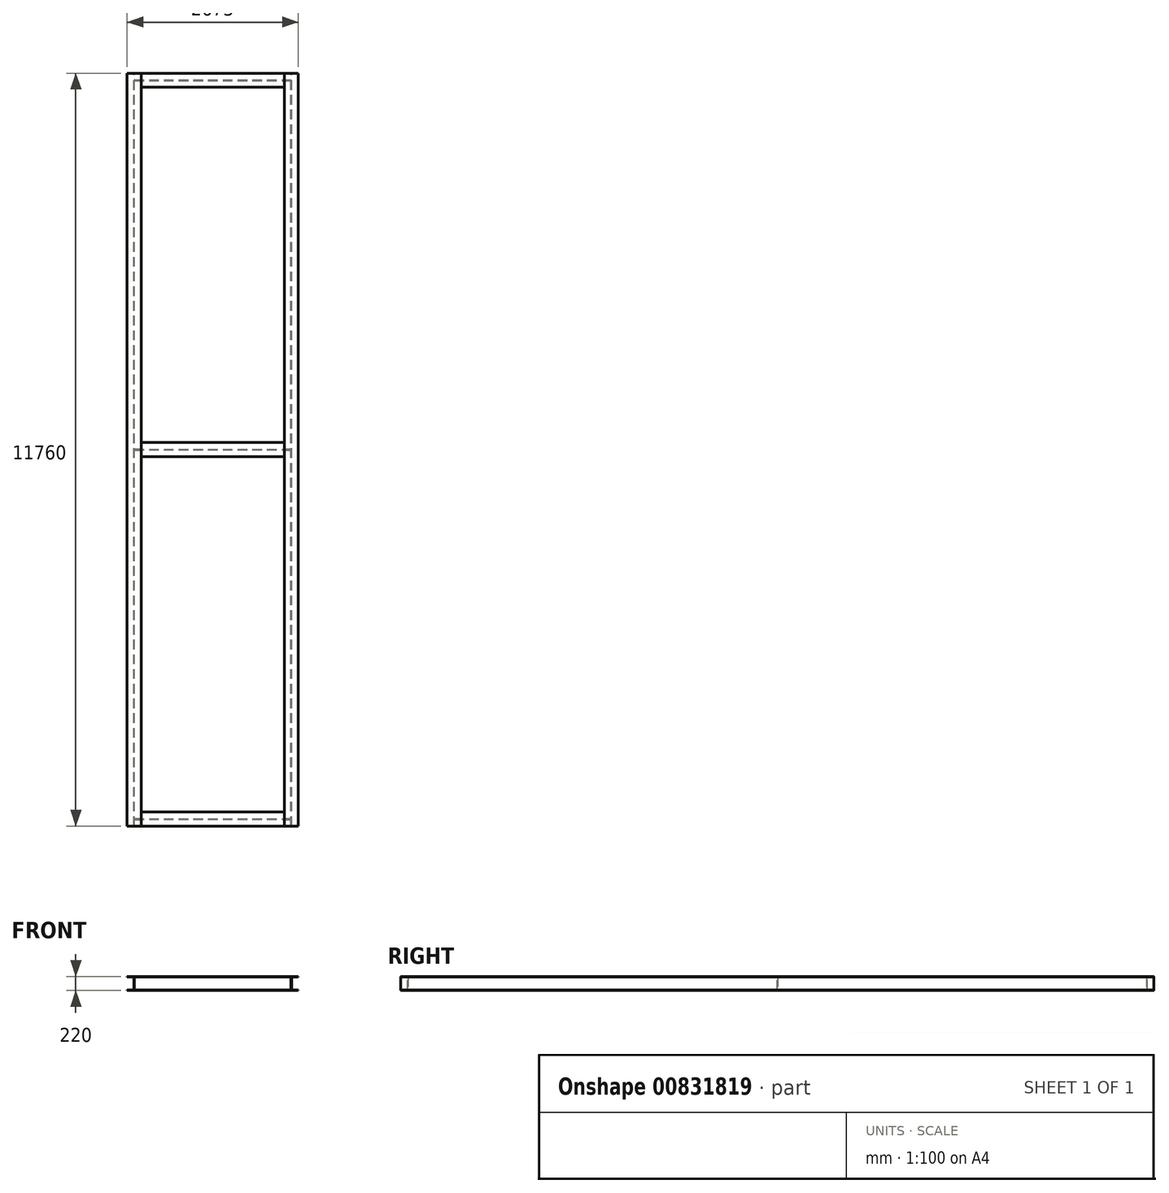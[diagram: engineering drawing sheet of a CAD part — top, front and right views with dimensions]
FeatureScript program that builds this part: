
annotation { "Feature Type Name" : "Feature", "Feature Type Description" : "" }
export const myFeature = defineFeature(function(context is Context, id is Id, definition is map)
    precondition{}
    {
        {
            var Q0;
            Q0=qCreatedBy(makeId("Front.planeOp"),FACE);
            var sketch = newSketch(context, id + "F0", { "sketchPlane" : qUnion([Q0])});
            skLineSegment(sketch, "E0", {"start": v(0, 0) * mm, "end": v(0, 110) * mm, "construction": true});
            skLineSegment(sketch, "E1", {"start": v(0, 0) * mm, "end": v(110, 0) * mm, "construction": true});
            skLineSegment(sketch, "E2", {"start": v(4, 0) * mm, "end": v(4, 97) * mm});
            skLineSegment(sketch, "E3", {"start": v(9, 102) * mm, "end": v(110, 102) * mm});
            skLineSegment(sketch, "E4", {"start": v(110, 102) * mm, "end": v(110, 110) * mm});
            skLineSegment(sketch, "E5", {"start": v(110, 110) * mm, "end": v(0, 110) * mm});
            skLineSegment(sketch, "E6.MirrorCS", {"start": v(-110, 110) * mm, "end": v(0, 110) * mm});
            skLineSegment(sketch, "E7.MirrorCS", {"start": v(-110, 102) * mm, "end": v(-110, 110) * mm});
            skLineSegment(sketch, "E8.MirrorCS", {"start": v(-9, 102) * mm, "end": v(-110, 102) * mm});
            skLineSegment(sketch, "E9.MirrorCS", {"start": v(-4, 0) * mm, "end": v(-4, 97) * mm});
            skLineSegment(sketch, "E10.MirrorCS", {"start": v(4, 0) * mm, "end": v(4, -97) * mm});
            skLineSegment(sketch, "E11.MirrorCS", {"start": v(9, -102) * mm, "end": v(110, -102) * mm});
            skLineSegment(sketch, "E12.MirrorCS", {"start": v(110, -102) * mm, "end": v(110, -110) * mm});
            skLineSegment(sketch, "E13.MirrorCS", {"start": v(110, -110) * mm, "end": v(0, -110) * mm});
            skLineSegment(sketch, "E14.MirrorCS", {"start": v(-110, -110) * mm, "end": v(0, -110) * mm});
            skLineSegment(sketch, "E15.MirrorCS", {"start": v(-110, -102) * mm, "end": v(-110, -110) * mm});
            skLineSegment(sketch, "E16.MirrorCS", {"start": v(-9, -102) * mm, "end": v(-110, -102) * mm});
            skLineSegment(sketch, "E17.MirrorCS", {"start": v(-4, 0) * mm, "end": v(-4, -97) * mm});
            skPoint(sketch, "E18.visualSharp", {"position": v(-4, 102) * mm});
            skArc(sketch, "E18.filletArc", {"start": v(-4, 97) * mm, "mid": v(-5.46, 100.54) * mm, "end": v(-9, 102) * mm});
            skPoint(sketch, "E19.visualSharp", {"position": v(4, 102) * mm});
            skArc(sketch, "E19.filletArc", {"start": v(9, 102) * mm, "mid": v(5.46, 100.54) * mm, "end": v(4, 97) * mm});
            skPoint(sketch, "E20.visualSharp", {"position": v(4, -102) * mm});
            skArc(sketch, "E20.filletArc", {"start": v(4, -97) * mm, "mid": v(5.46, -100.54) * mm, "end": v(9, -102) * mm});
            skPoint(sketch, "E21.visualSharp", {"position": v(-4, -102) * mm});
            skArc(sketch, "E21.filletArc", {"start": v(-9, -102) * mm, "mid": v(-5.46, -100.54) * mm, "end": v(-4, -97) * mm});
            skSolve(sketch);
        }
        {
            var Q0;
            Q0=makeQuery(id+"F0.imprint","IMPRINT",FACE,{"disambiguationData":[TD([[makeQuery(id+"F0.imprint","IMPRINT",EDGE,{"derivedFrom":sQuery(id+"F0.wireOp",EDGE,"E2")}),1.0]])]});
            extrude(context, id + "F1", {"entities" : qUnion([Q0]), "endBound" : BoundingType.SYMMETRIC, "depth" : 11760 * mm, "offsetDistance" : 25 * mm});
        }
        {
            var Q0;
            Q0=makeQuery(id+"F1.opExtrude","SWEPT_FACE",FACE,{"disambiguationData":[OSD([sQuery(id+"F0.wireOp",EDGE,"E9.MirrorCS"),sQuery(id+"F0.wireOp",EDGE,"E17.MirrorCS")])]});
            var sketch = newSketch(context, id + "F2", { "sketchPlane" : qUnion([Q0])});
            skLineSegment(sketch, "E22", {"start": v(5770, 0) * mm, "end": v(5770, 110) * mm, "construction": true});
            skLineSegment(sketch, "E23", {"start": v(5770, 0) * mm, "end": v(5880, 0) * mm, "construction": true});
            skLineSegment(sketch, "E24", {"start": v(5774, 0) * mm, "end": v(5774, 97) * mm});
            skLineSegment(sketch, "E25", {"start": v(5779, 102) * mm, "end": v(5880, 102) * mm});
            skLineSegment(sketch, "E26", {"start": v(5880, 102) * mm, "end": v(5880, 110) * mm});
            skLineSegment(sketch, "E27", {"start": v(5880, 110) * mm, "end": v(5770, 110) * mm});
            skLineSegment(sketch, "E28.MirrorCS", {"start": v(5660, 110) * mm, "end": v(5770, 110) * mm});
            skLineSegment(sketch, "E29.MirrorCS", {"start": v(5660, 102) * mm, "end": v(5660, 110) * mm});
            skLineSegment(sketch, "E30.MirrorCS", {"start": v(5761, 102) * mm, "end": v(5660, 102) * mm});
            skLineSegment(sketch, "E31.MirrorCS", {"start": v(5766, 0) * mm, "end": v(5766, 97) * mm});
            skLineSegment(sketch, "E32.MirrorCS", {"start": v(5774, 0) * mm, "end": v(5774, -97) * mm});
            skLineSegment(sketch, "E33.MirrorCS", {"start": v(5779, -102) * mm, "end": v(5880, -102) * mm});
            skLineSegment(sketch, "E34.MirrorCS", {"start": v(5880, -102) * mm, "end": v(5880, -110) * mm});
            skLineSegment(sketch, "E35.MirrorCS", {"start": v(5880, -110) * mm, "end": v(5770, -110) * mm});
            skLineSegment(sketch, "E36.MirrorCS", {"start": v(5660, -110) * mm, "end": v(5770, -110) * mm});
            skLineSegment(sketch, "E37.MirrorCS", {"start": v(5660, -102) * mm, "end": v(5660, -110) * mm});
            skLineSegment(sketch, "E38.MirrorCS", {"start": v(5761, -102) * mm, "end": v(5660, -102) * mm});
            skLineSegment(sketch, "E39.MirrorCS", {"start": v(5766, 0) * mm, "end": v(5766, -97) * mm});
            skPoint(sketch, "E40.visualSharp", {"position": v(5766, 102) * mm});
            skArc(sketch, "E40.filletArc", {"start": v(5766, 97) * mm, "mid": v(5764.54, 100.54) * mm, "end": v(5761, 102) * mm});
            skPoint(sketch, "E41.visualSharp", {"position": v(5774, 102) * mm});
            skArc(sketch, "E41.filletArc", {"start": v(5779, 102) * mm, "mid": v(5775.46, 100.54) * mm, "end": v(5774, 97) * mm});
            skPoint(sketch, "E42.visualSharp", {"position": v(5774, -102) * mm});
            skArc(sketch, "E42.filletArc", {"start": v(5774, -97) * mm, "mid": v(5775.46, -100.54) * mm, "end": v(5779, -102) * mm});
            skPoint(sketch, "E43.visualSharp", {"position": v(5766, -102) * mm});
            skArc(sketch, "E43.filletArc", {"start": v(5761, -102) * mm, "mid": v(5764.54, -100.54) * mm, "end": v(5766, -97) * mm});
            skSolve(sketch);
        }
        {
            var Q0;
            Q0 = qSketchRegion(id + "F2", true);
            extrude(context, id + "F3", {"entities" : qUnion([Q0]), "depth" : 2453 * mm, "offsetDistance" : 25 * mm});
        }
        {
            var Q0;
            Q0=qCreatedBy(makeId("Right.planeOp"),FACE);
            cPlane(context, id + "F4", {"entities" : qUnion([Q0]), "cplaneType" : CPlaneType.OFFSET, "offset" : (2453 / 2) * mm, "oppositeDirection" : true, "width" : 150 * mm, "height" : 150 * mm});
        }
        {
            var Q0;
            Q0=makeQuery(id+"F1.opExtrude","SWEPT_BODY",BODY,{"disambiguationData":[OSD([sQuery(id+"F0.wireOp",EDGE,"E2"),sQuery(id+"F0.wireOp",EDGE,"E3"),sQuery(id+"F0.wireOp",EDGE,"E4"),sQuery(id+"F0.wireOp",EDGE,"E5"),sQuery(id+"F0.wireOp",EDGE,"E6.MirrorCS"),sQuery(id+"F0.wireOp",EDGE,"E7.MirrorCS"),sQuery(id+"F0.wireOp",EDGE,"E8.MirrorCS"),sQuery(id+"F0.wireOp",EDGE,"E9.MirrorCS"),sQuery(id+"F0.wireOp",EDGE,"E10.MirrorCS"),sQuery(id+"F0.wireOp",EDGE,"E11.MirrorCS"),sQuery(id+"F0.wireOp",EDGE,"E12.MirrorCS"),sQuery(id+"F0.wireOp",EDGE,"E13.MirrorCS"),sQuery(id+"F0.wireOp",EDGE,"E14.MirrorCS"),sQuery(id+"F0.wireOp",EDGE,"E15.MirrorCS"),sQuery(id+"F0.wireOp",EDGE,"E16.MirrorCS"),sQuery(id+"F0.wireOp",EDGE,"E17.MirrorCS"),sQuery(id+"F0.wireOp",EDGE,"E18.filletArc"),sQuery(id+"F0.wireOp",EDGE,"E19.filletArc"),sQuery(id+"F0.wireOp",EDGE,"E20.filletArc"),sQuery(id+"F0.wireOp",EDGE,"E21.filletArc")])]});
            var Q1;
            Q1=qCreatedBy(id+"F4.planeOp",FACE);
            mirror(context, id + "F5", {"entities" : qUnion([Q0]), "mirrorPlane" : qUnion([Q1])});
        }
        {
            var Q0;
            Q0=makeQuery(id+"F1.opExtrude","SWEPT_BODY",BODY,{"disambiguationData":[OSD([sQuery(id+"F0.wireOp",EDGE,"E2"),sQuery(id+"F0.wireOp",EDGE,"E3"),sQuery(id+"F0.wireOp",EDGE,"E4"),sQuery(id+"F0.wireOp",EDGE,"E5"),sQuery(id+"F0.wireOp",EDGE,"E6.MirrorCS"),sQuery(id+"F0.wireOp",EDGE,"E7.MirrorCS"),sQuery(id+"F0.wireOp",EDGE,"E8.MirrorCS"),sQuery(id+"F0.wireOp",EDGE,"E9.MirrorCS"),sQuery(id+"F0.wireOp",EDGE,"E10.MirrorCS"),sQuery(id+"F0.wireOp",EDGE,"E11.MirrorCS"),sQuery(id+"F0.wireOp",EDGE,"E12.MirrorCS"),sQuery(id+"F0.wireOp",EDGE,"E13.MirrorCS"),sQuery(id+"F0.wireOp",EDGE,"E14.MirrorCS"),sQuery(id+"F0.wireOp",EDGE,"E15.MirrorCS"),sQuery(id+"F0.wireOp",EDGE,"E16.MirrorCS"),sQuery(id+"F0.wireOp",EDGE,"E17.MirrorCS"),sQuery(id+"F0.wireOp",EDGE,"E18.filletArc"),sQuery(id+"F0.wireOp",EDGE,"E19.filletArc"),sQuery(id+"F0.wireOp",EDGE,"E20.filletArc"),sQuery(id+"F0.wireOp",EDGE,"E21.filletArc")])]});
            var Q1;
            Q1=makeQuery(id+"F5.opPattern","COPY",BODY,{"derivedFrom":makeQuery(id+"F1.opExtrude","SWEPT_BODY",BODY,{"disambiguationData":[OSD([sQuery(id+"F0.wireOp",EDGE,"E2"),sQuery(id+"F0.wireOp",EDGE,"E3"),sQuery(id+"F0.wireOp",EDGE,"E4"),sQuery(id+"F0.wireOp",EDGE,"E5"),sQuery(id+"F0.wireOp",EDGE,"E6.MirrorCS"),sQuery(id+"F0.wireOp",EDGE,"E7.MirrorCS"),sQuery(id+"F0.wireOp",EDGE,"E8.MirrorCS"),sQuery(id+"F0.wireOp",EDGE,"E9.MirrorCS"),sQuery(id+"F0.wireOp",EDGE,"E10.MirrorCS"),sQuery(id+"F0.wireOp",EDGE,"E11.MirrorCS"),sQuery(id+"F0.wireOp",EDGE,"E12.MirrorCS"),sQuery(id+"F0.wireOp",EDGE,"E13.MirrorCS"),sQuery(id+"F0.wireOp",EDGE,"E14.MirrorCS"),sQuery(id+"F0.wireOp",EDGE,"E15.MirrorCS"),sQuery(id+"F0.wireOp",EDGE,"E16.MirrorCS"),sQuery(id+"F0.wireOp",EDGE,"E17.MirrorCS"),sQuery(id+"F0.wireOp",EDGE,"E18.filletArc"),sQuery(id+"F0.wireOp",EDGE,"E19.filletArc"),sQuery(id+"F0.wireOp",EDGE,"E20.filletArc"),sQuery(id+"F0.wireOp",EDGE,"E21.filletArc")])]}),"instanceName":"1"});
            var Q2;
            Q2=makeQuery(id+"F3.opExtrude","SWEPT_BODY",BODY,{"disambiguationData":[OSD([sQuery(id+"F2.wireOp",EDGE,"E24"),sQuery(id+"F2.wireOp",EDGE,"E25"),sQuery(id+"F2.wireOp",EDGE,"E26"),sQuery(id+"F2.wireOp",EDGE,"E27"),sQuery(id+"F2.wireOp",EDGE,"E28.MirrorCS"),sQuery(id+"F2.wireOp",EDGE,"E29.MirrorCS"),sQuery(id+"F2.wireOp",EDGE,"E30.MirrorCS"),sQuery(id+"F2.wireOp",EDGE,"E31.MirrorCS"),sQuery(id+"F2.wireOp",EDGE,"E32.MirrorCS"),sQuery(id+"F2.wireOp",EDGE,"E33.MirrorCS"),sQuery(id+"F2.wireOp",EDGE,"E34.MirrorCS"),sQuery(id+"F2.wireOp",EDGE,"E35.MirrorCS"),sQuery(id+"F2.wireOp",EDGE,"E36.MirrorCS"),sQuery(id+"F2.wireOp",EDGE,"E37.MirrorCS"),sQuery(id+"F2.wireOp",EDGE,"E38.MirrorCS"),sQuery(id+"F2.wireOp",EDGE,"E39.MirrorCS"),sQuery(id+"F2.wireOp",EDGE,"E40.filletArc"),sQuery(id+"F2.wireOp",EDGE,"E41.filletArc"),sQuery(id+"F2.wireOp",EDGE,"E42.filletArc"),sQuery(id+"F2.wireOp",EDGE,"E43.filletArc")])]});
            booleanBodies(context, id + "F6", {"operationType" : BooleanOperationType.SUBTRACTION, "tools" : qUnion([Q0, Q1]), "targets" : qUnion([Q2]), "keepTools" : true});
        }
        {
            var Q0;
            Q0=makeQuery(id+"F3.opExtrude","SWEPT_BODY",BODY,{"disambiguationData":[OSD([sQuery(id+"F2.wireOp",EDGE,"E24"),sQuery(id+"F2.wireOp",EDGE,"E25"),sQuery(id+"F2.wireOp",EDGE,"E26"),sQuery(id+"F2.wireOp",EDGE,"E27"),sQuery(id+"F2.wireOp",EDGE,"E28.MirrorCS"),sQuery(id+"F2.wireOp",EDGE,"E29.MirrorCS"),sQuery(id+"F2.wireOp",EDGE,"E30.MirrorCS"),sQuery(id+"F2.wireOp",EDGE,"E31.MirrorCS"),sQuery(id+"F2.wireOp",EDGE,"E32.MirrorCS"),sQuery(id+"F2.wireOp",EDGE,"E33.MirrorCS"),sQuery(id+"F2.wireOp",EDGE,"E34.MirrorCS"),sQuery(id+"F2.wireOp",EDGE,"E35.MirrorCS"),sQuery(id+"F2.wireOp",EDGE,"E36.MirrorCS"),sQuery(id+"F2.wireOp",EDGE,"E37.MirrorCS"),sQuery(id+"F2.wireOp",EDGE,"E38.MirrorCS"),sQuery(id+"F2.wireOp",EDGE,"E39.MirrorCS"),sQuery(id+"F2.wireOp",EDGE,"E40.filletArc"),sQuery(id+"F2.wireOp",EDGE,"E41.filletArc"),sQuery(id+"F2.wireOp",EDGE,"E42.filletArc"),sQuery(id+"F2.wireOp",EDGE,"E43.filletArc")])]});
            var Q1;
            Q1=qCreatedBy(makeId("Front.planeOp"),FACE);
            mirror(context, id + "F7", {"entities" : qUnion([Q0]), "mirrorPlane" : qUnion([Q1])});
        }
        {
            var Q0;
            Q0=makeQuery(id+"F1.opExtrude","SWEPT_FACE",FACE,{"disambiguationData":[OSD([sQuery(id+"F0.wireOp",EDGE,"E9.MirrorCS"),sQuery(id+"F0.wireOp",EDGE,"E17.MirrorCS")])]});
            var sketch = newSketch(context, id + "F8", { "sketchPlane" : qUnion([Q0])});
            skLineSegment(sketch, "E44", {"start": v(0, 0) * mm, "end": v(0, 110) * mm, "construction": true});
            skLineSegment(sketch, "E45", {"start": v(0, 0) * mm, "end": v(110, 0) * mm, "construction": true});
            skLineSegment(sketch, "E46", {"start": v(4, 0) * mm, "end": v(4, 97) * mm});
            skLineSegment(sketch, "E47", {"start": v(9, 102) * mm, "end": v(110, 102) * mm});
            skLineSegment(sketch, "E48", {"start": v(110, 102) * mm, "end": v(110, 110) * mm});
            skLineSegment(sketch, "E49", {"start": v(110, 110) * mm, "end": v(0, 110) * mm});
            skLineSegment(sketch, "E50.MirrorCS", {"start": v(-110, 110) * mm, "end": v(0, 110) * mm});
            skLineSegment(sketch, "E51.MirrorCS", {"start": v(-110, 102) * mm, "end": v(-110, 110) * mm});
            skLineSegment(sketch, "E52.MirrorCS", {"start": v(-9, 102) * mm, "end": v(-110, 102) * mm});
            skLineSegment(sketch, "E53.MirrorCS", {"start": v(-4, 0) * mm, "end": v(-4, 97) * mm});
            skLineSegment(sketch, "E54.MirrorCS", {"start": v(4, 0) * mm, "end": v(4, -97) * mm});
            skLineSegment(sketch, "E55.MirrorCS", {"start": v(9, -102) * mm, "end": v(110, -102) * mm});
            skLineSegment(sketch, "E56.MirrorCS", {"start": v(110, -102) * mm, "end": v(110, -110) * mm});
            skLineSegment(sketch, "E57.MirrorCS", {"start": v(110, -110) * mm, "end": v(0, -110) * mm});
            skLineSegment(sketch, "E58.MirrorCS", {"start": v(-110, -110) * mm, "end": v(0, -110) * mm});
            skLineSegment(sketch, "E59.MirrorCS", {"start": v(-110, -102) * mm, "end": v(-110, -110) * mm});
            skLineSegment(sketch, "E60.MirrorCS", {"start": v(-9, -102) * mm, "end": v(-110, -102) * mm});
            skLineSegment(sketch, "E61.MirrorCS", {"start": v(-4, 0) * mm, "end": v(-4, -97) * mm});
            skPoint(sketch, "E62.visualSharp", {"position": v(-4, 102) * mm});
            skArc(sketch, "E62.filletArc", {"start": v(-4, 97) * mm, "mid": v(-5.46, 100.54) * mm, "end": v(-9, 102) * mm});
            skPoint(sketch, "E63.visualSharp", {"position": v(4, 102) * mm});
            skArc(sketch, "E63.filletArc", {"start": v(9, 102) * mm, "mid": v(5.46, 100.54) * mm, "end": v(4, 97) * mm});
            skPoint(sketch, "E64.visualSharp", {"position": v(4, -102) * mm});
            skArc(sketch, "E64.filletArc", {"start": v(4, -97) * mm, "mid": v(5.46, -100.54) * mm, "end": v(9, -102) * mm});
            skPoint(sketch, "E65.visualSharp", {"position": v(-4, -102) * mm});
            skArc(sketch, "E65.filletArc", {"start": v(-9, -102) * mm, "mid": v(-5.46, -100.54) * mm, "end": v(-4, -97) * mm});
            skSolve(sketch);
        }
        {
            var Q0;
            Q0 = qSketchRegion(id + "F8", true);
            var Q1;
            Q1=makeQuery(id+"F5.opPattern","COPY",FACE,{"derivedFrom":makeQuery(id+"F1.opExtrude","SWEPT_FACE",FACE,{"disambiguationData":[OSD([sQuery(id+"F0.wireOp",EDGE,"E9.MirrorCS"),sQuery(id+"F0.wireOp",EDGE,"E17.MirrorCS")])]}),"instanceName":"1"});
            extrude(context, id + "F9", {"entities" : qUnion([Q0]), "endBound" : BoundingType.UP_TO_SURFACE, "depth" : 25 * mm, "endBoundEntityFace" : qUnion([Q1]), "offsetDistance" : 25 * mm});
        }
        {
            var Q0;
            Q0=makeQuery(id+"F5.opPattern","COPY",BODY,{"derivedFrom":makeQuery(id+"F1.opExtrude","SWEPT_BODY",BODY,{"disambiguationData":[OSD([sQuery(id+"F0.wireOp",EDGE,"E2"),sQuery(id+"F0.wireOp",EDGE,"E3"),sQuery(id+"F0.wireOp",EDGE,"E4"),sQuery(id+"F0.wireOp",EDGE,"E5"),sQuery(id+"F0.wireOp",EDGE,"E6.MirrorCS"),sQuery(id+"F0.wireOp",EDGE,"E7.MirrorCS"),sQuery(id+"F0.wireOp",EDGE,"E8.MirrorCS"),sQuery(id+"F0.wireOp",EDGE,"E9.MirrorCS"),sQuery(id+"F0.wireOp",EDGE,"E10.MirrorCS"),sQuery(id+"F0.wireOp",EDGE,"E11.MirrorCS"),sQuery(id+"F0.wireOp",EDGE,"E12.MirrorCS"),sQuery(id+"F0.wireOp",EDGE,"E13.MirrorCS"),sQuery(id+"F0.wireOp",EDGE,"E14.MirrorCS"),sQuery(id+"F0.wireOp",EDGE,"E15.MirrorCS"),sQuery(id+"F0.wireOp",EDGE,"E16.MirrorCS"),sQuery(id+"F0.wireOp",EDGE,"E17.MirrorCS"),sQuery(id+"F0.wireOp",EDGE,"E18.filletArc"),sQuery(id+"F0.wireOp",EDGE,"E19.filletArc"),sQuery(id+"F0.wireOp",EDGE,"E20.filletArc"),sQuery(id+"F0.wireOp",EDGE,"E21.filletArc")])]}),"instanceName":"1"});
            var Q1;
            Q1=makeQuery(id+"F1.opExtrude","SWEPT_BODY",BODY,{"disambiguationData":[OSD([sQuery(id+"F0.wireOp",EDGE,"E2"),sQuery(id+"F0.wireOp",EDGE,"E3"),sQuery(id+"F0.wireOp",EDGE,"E4"),sQuery(id+"F0.wireOp",EDGE,"E5"),sQuery(id+"F0.wireOp",EDGE,"E6.MirrorCS"),sQuery(id+"F0.wireOp",EDGE,"E7.MirrorCS"),sQuery(id+"F0.wireOp",EDGE,"E8.MirrorCS"),sQuery(id+"F0.wireOp",EDGE,"E9.MirrorCS"),sQuery(id+"F0.wireOp",EDGE,"E10.MirrorCS"),sQuery(id+"F0.wireOp",EDGE,"E11.MirrorCS"),sQuery(id+"F0.wireOp",EDGE,"E12.MirrorCS"),sQuery(id+"F0.wireOp",EDGE,"E13.MirrorCS"),sQuery(id+"F0.wireOp",EDGE,"E14.MirrorCS"),sQuery(id+"F0.wireOp",EDGE,"E15.MirrorCS"),sQuery(id+"F0.wireOp",EDGE,"E16.MirrorCS"),sQuery(id+"F0.wireOp",EDGE,"E17.MirrorCS"),sQuery(id+"F0.wireOp",EDGE,"E18.filletArc"),sQuery(id+"F0.wireOp",EDGE,"E19.filletArc"),sQuery(id+"F0.wireOp",EDGE,"E20.filletArc"),sQuery(id+"F0.wireOp",EDGE,"E21.filletArc")])]});
            var Q2;
            Q2=makeQuery(id+"F9.opExtrude","SWEPT_BODY",BODY,{"disambiguationData":[OSD([sQuery(id+"F8.wireOp",EDGE,"E46"),sQuery(id+"F8.wireOp",EDGE,"E47"),sQuery(id+"F8.wireOp",EDGE,"E48"),sQuery(id+"F8.wireOp",EDGE,"E49"),sQuery(id+"F8.wireOp",EDGE,"E50.MirrorCS"),sQuery(id+"F8.wireOp",EDGE,"E51.MirrorCS"),sQuery(id+"F8.wireOp",EDGE,"E52.MirrorCS"),sQuery(id+"F8.wireOp",EDGE,"E53.MirrorCS"),sQuery(id+"F8.wireOp",EDGE,"E54.MirrorCS"),sQuery(id+"F8.wireOp",EDGE,"E55.MirrorCS"),sQuery(id+"F8.wireOp",EDGE,"E56.MirrorCS"),sQuery(id+"F8.wireOp",EDGE,"E57.MirrorCS"),sQuery(id+"F8.wireOp",EDGE,"E58.MirrorCS"),sQuery(id+"F8.wireOp",EDGE,"E59.MirrorCS"),sQuery(id+"F8.wireOp",EDGE,"E60.MirrorCS"),sQuery(id+"F8.wireOp",EDGE,"E61.MirrorCS"),sQuery(id+"F8.wireOp",EDGE,"E62.filletArc"),sQuery(id+"F8.wireOp",EDGE,"E63.filletArc"),sQuery(id+"F8.wireOp",EDGE,"E64.filletArc"),sQuery(id+"F8.wireOp",EDGE,"E65.filletArc")])]});
            booleanBodies(context, id + "F10", {"operationType" : BooleanOperationType.SUBTRACTION, "tools" : qUnion([Q0, Q1]), "targets" : qUnion([Q2]), "keepTools" : true});
        }
    });
